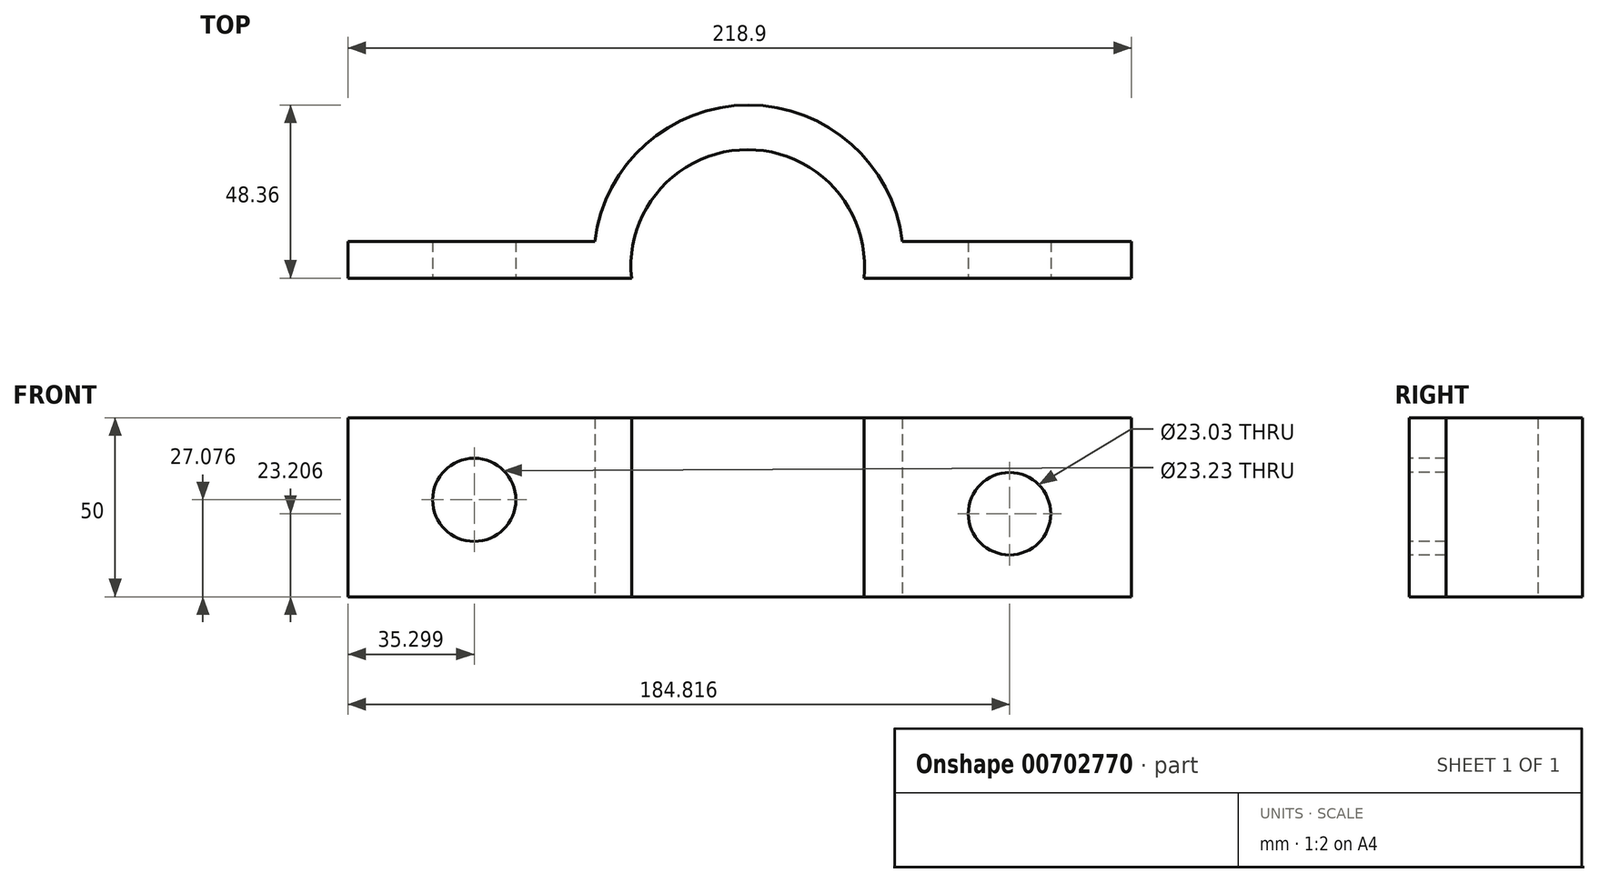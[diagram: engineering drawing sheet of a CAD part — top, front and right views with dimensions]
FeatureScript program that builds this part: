
annotation { "Feature Type Name" : "Feature", "Feature Type Description" : "" }
export const myFeature = defineFeature(function(context is Context, id is Id, definition is map)
    precondition{}
    {
        {
            var Q0;
            Q0=qCreatedBy(makeId("Top.planeOp"),FACE);
            var sketch = newSketch(context, id + "F0", { "sketchPlane" : qUnion([Q0])});
            skLineSegment(sketch, "E0", {"start": v(-174.81, 17.46) * mm, "end": v(-105.87, 17.46) * mm});
            skArc(sketch, "E1", {"start": v(-19.92, 17.46) * mm, "mid": v(-62.9, 55.52) * mm, "end": v(-105.87, 17.46) * mm});
            skLineSegment(sketch, "E2", {"start": v(-19.92, 17.46) * mm, "end": v(44.1, 17.46) * mm});
            skLineSegment(sketch, "E3", {"start": v(44.1, 17.46) * mm, "end": v(44.1, 7.16) * mm});
            skLineSegment(sketch, "E4", {"start": v(44.1, 7.16) * mm, "end": v(-30.66, 7.16) * mm});
            skArc(sketch, "E5", {"start": v(-30.66, 7.16) * mm, "mid": v(-63.12, 43.08) * mm, "end": v(-95.57, 7.16) * mm});
            skLineSegment(sketch, "E6", {"start": v(-95.57, 7.16) * mm, "end": v(-174.81, 7.16) * mm});
            skLineSegment(sketch, "E7", {"start": v(-174.81, 7.16) * mm, "end": v(-174.81, 17.46) * mm});
            skSolve(sketch);
        }
        {
            var Q0;
            Q0 = qSketchRegion(id + "F0", true);
            extrude(context, id + "F1", {"entities" : qUnion([Q0]), "depth" : 50 * mm, "offsetDistance" : 25 * mm});
        }
        {
            var Q0;
            Q0=makeQuery(id+"F1.opExtrude","SWEPT_FACE",FACE,{"disambiguationData":[OSD([sQuery(id+"F0.wireOp",EDGE,"E6")])]});
            var sketch = newSketch(context, id + "F2", { "sketchPlane" : qUnion([Q0])});
            skCircle(sketch, "E8", {"center": v(-139.51, 27.08) * mm, "radius": 11.62 * mm});
            skCircle(sketch, "E9", {"center": v(10, 23.2) * mm, "radius": 11.52 * mm});
            skSolve(sketch);
        }
        {
            var Q0;
            Q0 = qSketchRegion(id + "F2", true);
            extrude(context, id + "F3", {"entities" : qUnion([Q0]), "operationType" : NewBodyOperationType.REMOVE, "oppositeDirection" : true, "depth" : 50 * mm, "offsetDistance" : 25 * mm});
        }
    });
